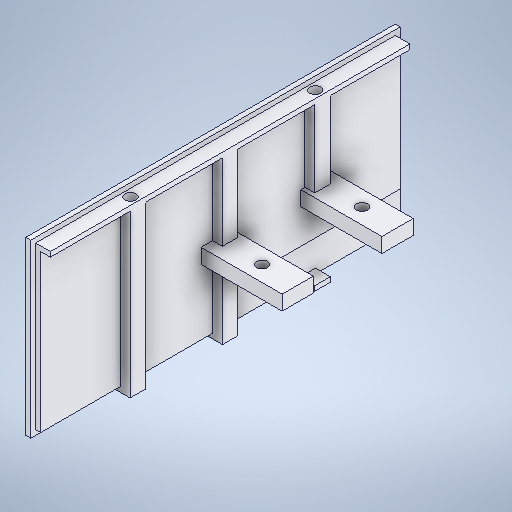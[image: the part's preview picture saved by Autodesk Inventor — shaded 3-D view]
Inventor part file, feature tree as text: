
AUTODESK INVENTOR PART (.ipt)
format: ipt  version: 2025 (Build 290162000, 162)  size: 483,328 bytes
history: native  units: in
note: dims shown in document units (in); Inventor stores cm internally (conversion verified against a paired STEP export)
features: projected_geometry x18, extrude x11, sketch x11
ambient origin geometry x8: Origin, YZ Plane, XZ Plane, XY Plane, X Axis, Y Axis, Z Axis, Center Point
bodies: Solid1 (feature_tree)
feature tree (40):
  extrude  "Extrusion1"  Depth=5.9213in
  extrude  "Extrusion2"  Depth=0.0787in
  extrude  "Extrusion3"  Depth=0.0787in
  extrude  "Extrusion4"  Depth=0.25in
  extrude  "Extrusion5"  Depth=0.25in
  extrude  "Extrusion6"  Depth=0.0787in TaperAngle=0.0deg
  extrude  "Extrusion10"  Depth=1.05in
  extrude  "Extrusion11"  Depth=1.3in
  extrude  "Extrusion12"  Depth=0.25in
  extrude  "Extrusion13"  Depth=0.2362in
  extrude  "Extrusion14"  Depth=0.5in
  sketch  "Sketch1"  dims[d0=2.75in d1=5.9213in]
  sketch  "Sketch2"  dims[d2=0.0787in d3=0.0in d4=0.0787in]
  projected_geometry  "Projected Loop1"
  sketch  "Sketch3"  dims[d5=0.0787in d6=0.0787in]
  projected_geometry  "Projected Loop2"
  sketch  "Sketch4"  dims[d7=0.0787in d8=0.0in d9=0.25in]
  projected_geometry  "Projected Loop3"
  sketch  "Sketch5"  dims[d10=0.25in d11=0.25in]
  projected_geometry  "Projected Loop4"
  sketch  "Sketch6"  dims[d12=0.1575in d13=0.0in d14=0.0787in d15=0.0in]
  projected_geometry  "Projected Loop5"
  projected_geometry  "Projected Loop6"
  projected_geometry  "Projected Loop7"
  projected_geometry  "Projected Loop8"
  sketch  "Sketch12"  dims[d16=0.0787in d17=0.0in d18=1.05in]
  projected_geometry  "Projected Loop12"
  projected_geometry  "Projected Loop13"
  sketch  "Sketch13"  dims[d22=1.3in d23=0.0in d31=0.8in]
  projected_geometry  "Projected Loop14"
  projected_geometry  "Projected Loop15"
  sketch  "Sketch14"  dims[d32=1.6in d33=0.25in]
  projected_geometry  "Projected Loop16"
  projected_geometry  "Projected Loop17"
  projected_geometry  "Projected Loop18"
  sketch  "Sketch15"  dims[d34=0.5in d35=0.2362in]
  projected_geometry  "Projected Loop19"
  projected_geometry  "Projected Loop20"
  sketch  "Sketch16"  dims[d36=0.25in d37=0.5in d38=0.2362in d39=0.1772in d40=0.1772in d41=0.1969in d42=0.0in d43=1.0in d44=0.0in d45=0.0787in d46=0.0in d47=0.1772in d48=0.1772in d49=0.1969in d50=0.0in d51=0.5in d52=0.0787in d53=0.0in d29=0.5in d30=0.0344in]
  projected_geometry  "Projected Loop21"
